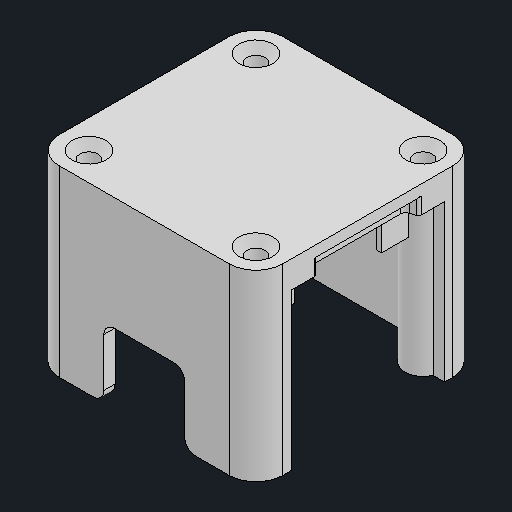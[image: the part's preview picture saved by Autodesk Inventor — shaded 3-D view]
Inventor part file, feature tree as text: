
AUTODESK INVENTOR PART (.ipt)
format: ipt  version: 2024.2 (Build 282272000, 272)  size: 201,728 bytes
history: native  units: mm
features: other x1, extrude x1
ambient origin geometry x8: Origin, YZ Plane, XZ Plane, XY Plane, X Axis, Y Axis, Z Axis, Center Point
bodies: Body1 (feature_tree)
feature tree (2):
  other  "솔리드1"
  extrude  "Extrude-Thin5"  [1 undecoded]
note: 1 required parameter value undecoded (feature->parameter linkage not recoverable at this tier; creation-order binding heuristic only, values carry confidence <= 0.55)
